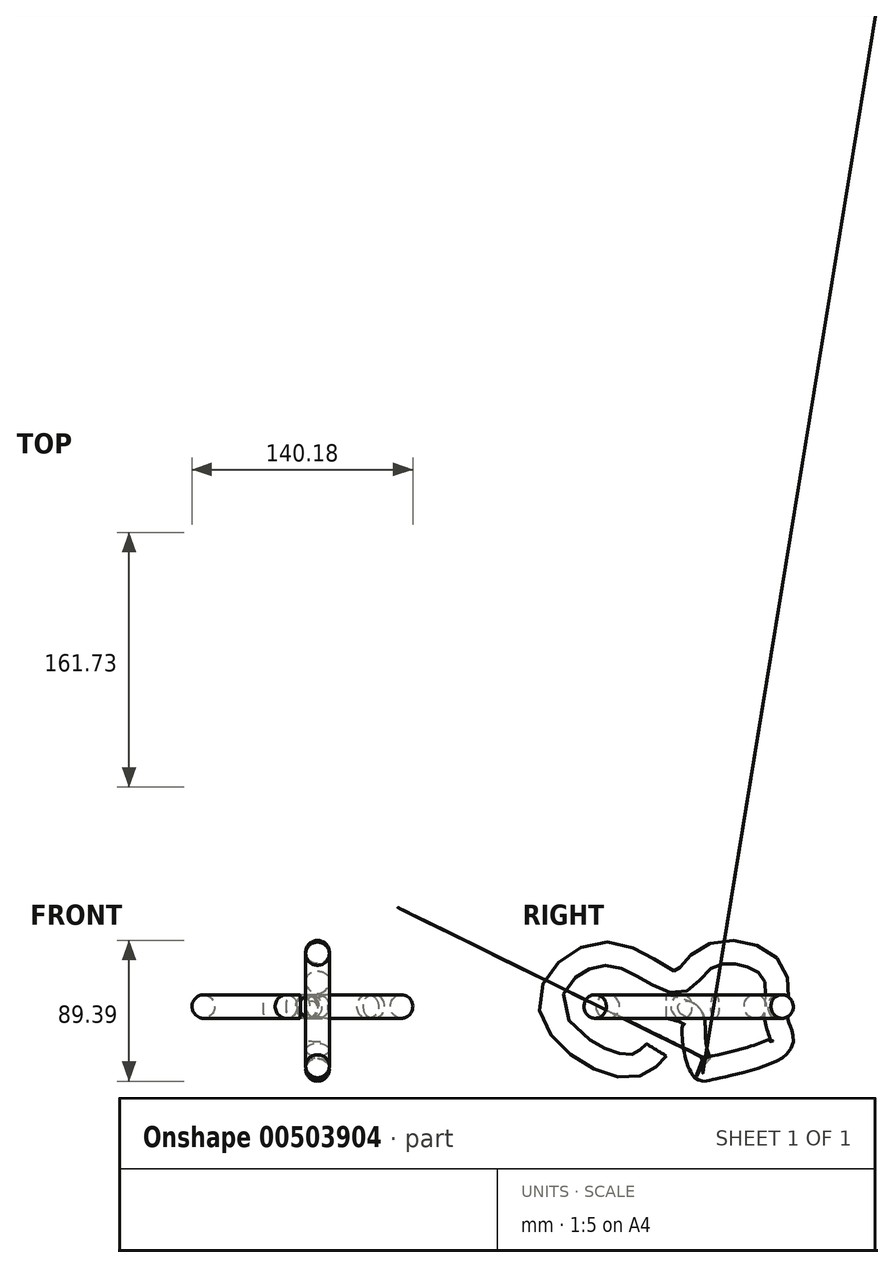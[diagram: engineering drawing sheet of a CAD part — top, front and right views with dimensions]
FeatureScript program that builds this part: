
annotation { "Feature Type Name" : "Feature", "Feature Type Description" : "" }
export const myFeature = defineFeature(function(context is Context, id is Id, definition is map)
    precondition{}
    {
        {
            var Q0;
            Q0=qCreatedBy(makeId("Front.planeOp"),FACE);
            var sketch = newSketch(context, id + "F0", { "sketchPlane" : qUnion([Q0])});
            skCircle(sketch, "E0", {"center": v(0, 0) * mm, "radius": 7.5 * mm});
            skSolve(sketch);
        }
        {
            var Q0;
            Q0=qCreatedBy(makeId("Top.planeOp"),FACE);
            var sketch = newSketch(context, id + "F1", { "sketchPlane" : qUnion([Q0])});
            skFitSpline(sketch, "E1", {"points": [v(0, 0) * mm, v(-3.48, -25.98) * mm, v(13.13, -43.4) * mm, v(33.48, -42.86) * mm, v(48.48, -30) * mm, v(53.04, -4.29) * mm, v(49.82, 15.8) * mm, v(32.41, 35.9) * mm, v(34.82, 62.68) * mm, v(9.38, 73.4) * mm, v(-13.4, 67.5) * mm, v(-19.55, 53.04) * mm, v(-13.12, 40.18) * mm, v(-6.96, 31.07) * mm], "startDerivative": vector(-102.03, -316.13) * mm, "endDerivative": vector(103.9, -158.16) * mm});
            skFitSpline(sketch, "E2", {"points": [v(-6.96, 31.07) * mm, v(-6.96, 20.9) * mm, v(-17.14, 10.18) * mm, v(-31.88, 25.98) * mm, v(-42.59, 53.57) * mm, v(-67.5, 50.63) * mm, v(-70.71, 19.29) * mm, v(-62.41, 0) * mm, v(-47.14, -10.45) * mm, v(-31.88, -13.13) * mm, v(-23.84, -30.54) * mm, v(-11.25, -37.23) * mm], "startDerivative": vector(28.18, -144.48) * mm, "endDerivative": vector(187.64, -47) * mm});
            skFitSpline(sketch, "E3", {"points": [v(-11.25, -37.23) * mm, v(12.05, -25.98) * mm, v(21.43, 11.79) * mm, v(43.93, 31.07) * mm, v(61.6, 50.36) * mm], "startDerivative": vector(120.91, 24.01) * mm, "endDerivative": vector(66.84, 88.9) * mm});
            skSolve(sketch);
        }
        {
            var Q0;
            Q0=makeQuery(id+"F0.imprint","IMPRINT",FACE,{"disambiguationData":[TD([[makeQuery(id+"F0.imprint","IMPRINT",EDGE,{"derivedFrom":sQuery(id+"F0.wireOp",EDGE,"E0")}),1.0]])]});
            var Q1;
            Q1=sQuery(id+"F1.wireOp",EDGE,"E1");
            var Q2;
            Q2=sQuery(id+"F1.wireOp",EDGE,"E2");
            sweep(context, id + "F2", {"profiles" : qUnion([Q0]), "path" : qUnion([Q1, Q2])});
        }
        {
            var Q0;
            Q0=qCreatedBy(makeId("Right.planeOp"),FACE);
            var sketch = newSketch(context, id + "F3", { "sketchPlane" : qUnion([Q0])});
            skFitSpline(sketch, "E4", {"points": [v(0, 0) * mm, v(15.66, -6.16) * mm, v(17.54, -20.36) * mm, v(22.63, -39.1) * mm, v(27.45, -39.38) * mm, v(71.91, -24.38) * mm, v(70.04, -8.84) * mm, v(67.1, 23.04) * mm, v(27.45, 32.14) * mm, v(7.1, 15.8) * mm, v(-37.37, 33.48) * mm, v(-73.53, 0) * mm, v(-26.66, -37.77) * mm, v(-6.3, -27.59) * mm], "startDerivative": vector(329.52, -69.39) * mm, "endDerivative": vector(225.95, 237.79) * mm});
            skSolve(sketch);
        }
        {
            var Q0;
            Q0=makeQuery(id+"F2.opSweep","CAP_FACE",FACE,{"disambiguationData":[OSD([sQuery(id+"F0.wireOp",EDGE,"E0"),sQuery(id+"F1.wireOp",VERTEX,"E1.start")])],"isStart":true});
            var Q1;
            Q1=sQuery(id+"F3.wireOp",EDGE,"E4");
            sweep(context, id + "F4", {"operationType" : NewBodyOperationType.ADD, "profiles" : qUnion([Q0]), "path" : qUnion([Q1])});
        }
    });
